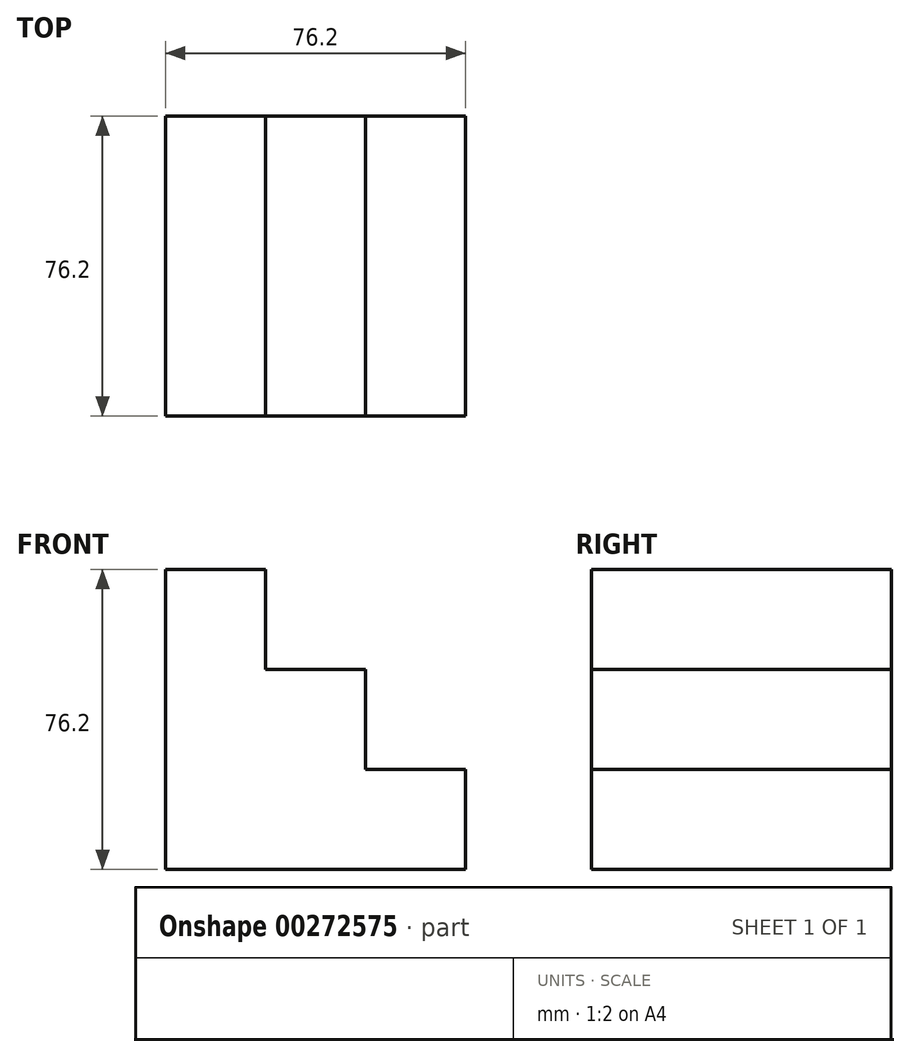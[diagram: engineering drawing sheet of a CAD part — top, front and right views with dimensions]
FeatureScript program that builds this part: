
annotation { "Feature Type Name" : "Feature", "Feature Type Description" : "" }
export const myFeature = defineFeature(function(context is Context, id is Id, definition is map)
    precondition{}
    {
        {
            var Q0;
            Q0=qCreatedBy(makeId("Front.planeOp"),FACE);
            var sketch = newSketch(context, id + "F0", { "sketchPlane" : qUnion([Q0])});
            skLineSegment(sketch, "E0", {"start": v(0, 0) * mm, "end": v(-76.2, 0) * mm});
            skLineSegment(sketch, "E1", {"start": v(-76.2, 0) * mm, "end": v(-76.2, 76.2) * mm});
            skLineSegment(sketch, "E2", {"start": v(-76.2, 76.2) * mm, "end": v(-50.8, 76.2) * mm});
            skLineSegment(sketch, "E3", {"start": v(-50.8, 76.2) * mm, "end": v(-50.8, 50.8) * mm});
            skLineSegment(sketch, "E4", {"start": v(-50.8, 50.8) * mm, "end": v(-25.4, 50.8) * mm});
            skLineSegment(sketch, "E5", {"start": v(-25.4, 50.8) * mm, "end": v(-25.4, 25.4) * mm});
            skLineSegment(sketch, "E6", {"start": v(-25.4, 25.4) * mm, "end": v(0, 25.4) * mm});
            skLineSegment(sketch, "E7", {"start": v(0, 25.4) * mm, "end": v(0, 0) * mm});
            skSolve(sketch);
        }
        {
            var Q0;
            Q0 = qSketchRegion(id + "F0", true);
            extrude(context, id + "F1", {"entities" : qUnion([Q0]), "depth" : 76.2 * mm});
        }
    });
